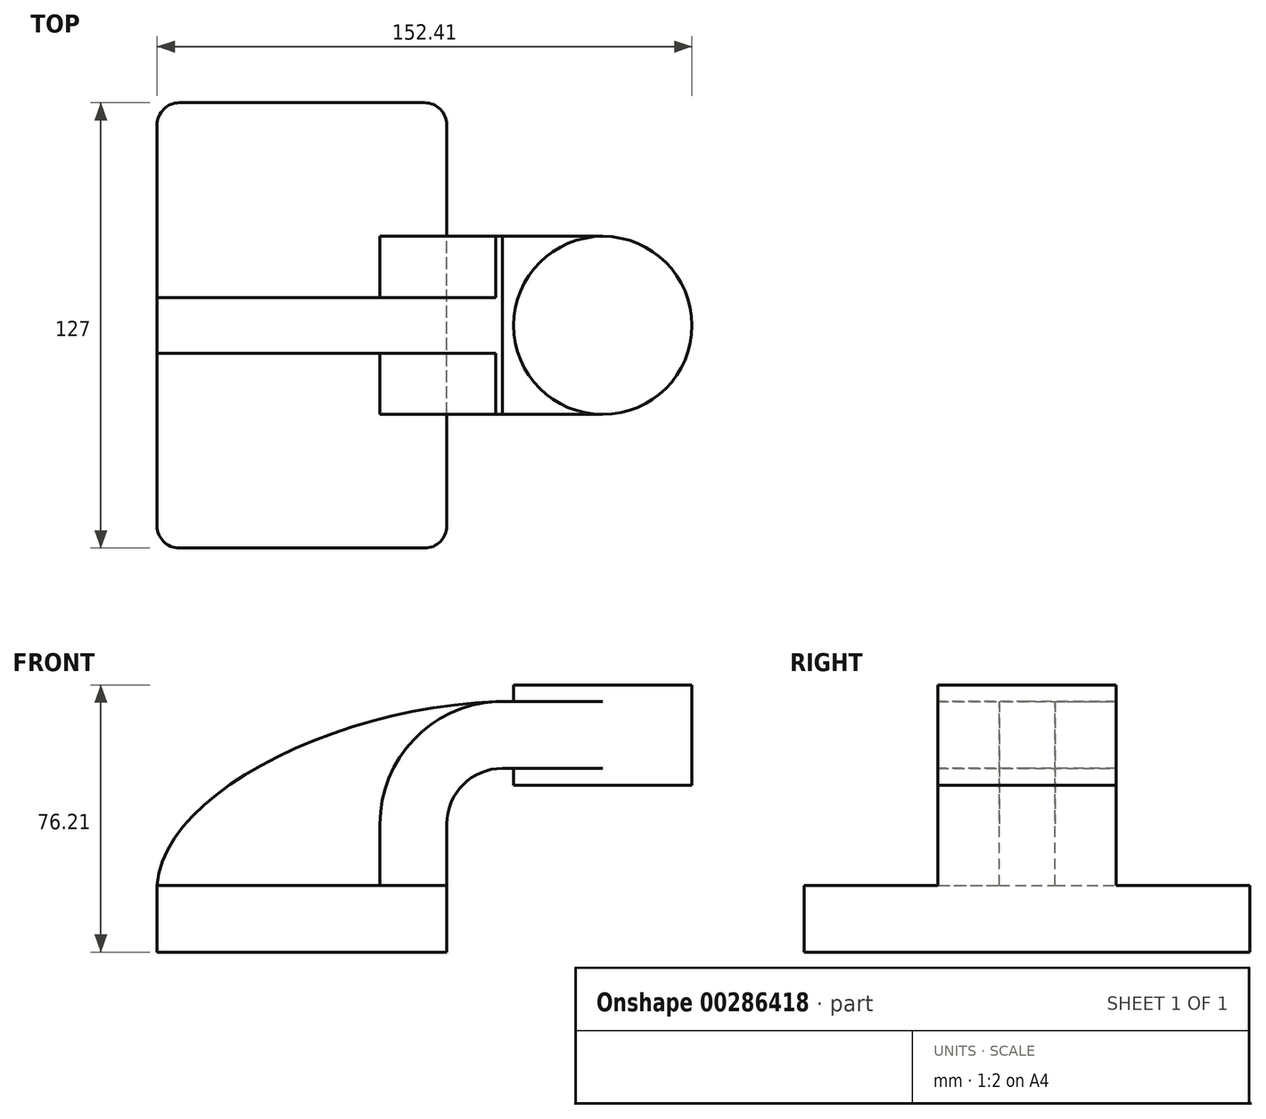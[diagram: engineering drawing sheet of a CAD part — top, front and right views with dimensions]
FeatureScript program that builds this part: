
annotation { "Feature Type Name" : "Feature", "Feature Type Description" : "" }
export const myFeature = defineFeature(function(context is Context, id is Id, definition is map)
    precondition{}
    {
        {
            var Q0;
            Q0=qCreatedBy(makeId("Front.planeOp"),FACE);
            var sketch = newSketch(context, id + "F0", { "sketchPlane" : qUnion([Q0])});
            skLineSegment(sketch, "E0.bottom", {"start": v(-41.27, -9.53) * mm, "end": v(41.28, -9.53) * mm});
            skLineSegment(sketch, "E0.top", {"start": v(-41.28, 9.52) * mm, "end": v(41.28, 9.52) * mm});
            skLineSegment(sketch, "E0.left", {"start": v(-41.28, -9.53) * mm, "end": v(-41.28, 9.52) * mm});
            skLineSegment(sketch, "E0.right", {"start": v(41.28, -9.53) * mm, "end": v(41.28, 9.52) * mm});
            skPoint(sketch, "E0.middle", {"position": v(0, 0) * mm});
            skLineSegment(sketch, "E1.bottom", {"start": v(60.32, 38.1) * mm, "end": v(111.12, 38.1) * mm});
            skLineSegment(sketch, "E1.top", {"start": v(60.32, 66.67) * mm, "end": v(111.12, 66.67) * mm});
            skLineSegment(sketch, "E1.left", {"start": v(60.32, 38.1) * mm, "end": v(60.32, 66.67) * mm});
            skLineSegment(sketch, "E1.right", {"start": v(111.12, 38.1) * mm, "end": v(111.12, 66.67) * mm});
            skPoint(sketch, "E1.middle", {"position": v(85.72, 52.39) * mm});
            skLineSegment(sketch, "E2", {"start": v(41.27, 9.52) * mm, "end": v(41.27, 27) * mm});
            skArc(sketch, "E3", {"start": v(41.27, 27) * mm, "mid": v(45.92, 38.23) * mm, "end": v(57.15, 42.88) * mm});
            skLineSegment(sketch, "E4", {"start": v(57.15, 42.88) * mm, "end": v(85.72, 42.88) * mm});
            skLineSegment(sketch, "E5.0", {"start": v(57.15, 61.93) * mm, "end": v(85.72, 61.93) * mm});
            skArc(sketch, "E5.1", {"start": v(22.22, 27) * mm, "mid": v(32.45, 51.7) * mm, "end": v(57.15, 61.93) * mm});
            skLineSegment(sketch, "E5.2", {"start": v(22.22, 9.52) * mm, "end": v(22.22, 27) * mm});
            skLineSegment(sketch, "E6", {"start": v(85.72, 38.1) * mm, "end": v(85.72, 66.67) * mm});
            skFitSpline(sketch, "E7", {"points": [v(-41.28, 9.53) * mm, v(57.15, 61.93) * mm], "startDerivative": vector(4.86, 79.85) * mm, "endDerivative": vector(136.77, 2.72) * mm});
            skSolve(sketch);
        }
        {
            var Q0;
            Q0=makeQuery(id+"F0.imprint","IMPRINT",FACE,{"disambiguationData":[TD([[makeQuery(id+"F0.imprint","IMPRINT",EDGE,{"derivedFrom":sQuery(id+"F0.wireOp",EDGE,"E0.bottom")}),1.0]])]});
            extrude(context, id + "F1", {"entities" : qUnion([Q0]), "endBound" : BoundingType.SYMMETRIC, "depth" : 127 * mm});
        }
        {
            var Q0;
            {var subQ1=sQuery(id+"F0.wireOp",EDGE,"E2");Q0=makeQuery(id+"F0.imprint","IMPRINT",FACE,{"disambiguationData":[TD([[makeQuery(id+"F0.imprint","IMPRINT",EDGE,{"derivedFrom":subQ1}),1.0]])]});}
            var Q1;
            {var subQ0=sQuery(id+"F0.wireOp",EDGE,"E4");var subQ1=sQuery(id+"F0.wireOp",EDGE,"E1.left");var subQ2=makeQuery(id+"F0.imprint","INTERSECT",VERTEX,{"derivedFrom":[subQ1,subQ0]});Q1=makeQuery(id+"F0.imprint","IMPRINT",FACE,{"disambiguationData":[TD([[makeQuery(id+"F0.imprint","IMPRINT",EDGE,{"disambiguationData":[TD([[subQ2,-1.0]])],"derivedFrom":subQ1}),-1.0]])]});}
            extrude(context, id + "F2", {"entities" : qUnion([Q0, Q1]), "operationType" : NewBodyOperationType.ADD, "endBound" : BoundingType.SYMMETRIC, "depth" : 50.8 * mm});
        }
        {
            var Q0;
            {var subQ3=sQuery(id+"F0.wireOp",EDGE,"E5.2");Q0=makeQuery(id+"F0.imprint","IMPRINT",FACE,{"disambiguationData":[TD([[makeQuery(id+"F0.imprint","IMPRINT",EDGE,{"derivedFrom":subQ3}),1.0]])]});}
            extrude(context, id + "F3", {"entities" : qUnion([Q0]), "operationType" : NewBodyOperationType.ADD, "endBound" : BoundingType.SYMMETRIC, "depth" : 15.88 * mm});
        }
        {
            var Q0;
            {var subQ4=sQuery(id+"F0.wireOp",EDGE,"E1.right");Q0=makeQuery(id+"F0.imprint","IMPRINT",FACE,{"disambiguationData":[TD([[makeQuery(id+"F0.imprint","IMPRINT",EDGE,{"derivedFrom":subQ4}),1.0]])]});}
            var Q1;
            Q1=sQuery(id+"F0.wireOp",EDGE,"E6");
            revolve(context, id + "F4", {"operationType" : NewBodyOperationType.ADD, "entities" : qUnion([Q0]), "axis" : qUnion([Q1]), "revolveType" : RevolveType.FULL});
        }
        {
            var Q0;
            Q0=makeQuery(id+"F1.opExtrude","CAP_EDGE",EDGE,{"disambiguationData":[OSD([sQuery(id+"F0.wireOp",EDGE,"E0.right")])],"isStart":false});
            var Q1;
            Q1=makeQuery(id+"F1.opExtrude","CAP_EDGE",EDGE,{"disambiguationData":[OSD([sQuery(id+"F0.wireOp",EDGE,"E0.right")])],"isStart":true});
            var Q2;
            Q2=makeQuery(id+"F1.opExtrude","CAP_EDGE",EDGE,{"disambiguationData":[OSD([sQuery(id+"F0.wireOp",EDGE,"E0.left")])],"isStart":true});
            var Q3;
            Q3=makeQuery(id+"F1.opExtrude","CAP_EDGE",EDGE,{"disambiguationData":[OSD([sQuery(id+"F0.wireOp",EDGE,"E0.left")])],"isStart":false});
            fillet(context, id + "F5", {"entities" : qUnion([Q0, Q1, Q2, Q3]), "radius" : 6.35 * mm, "tangentPropagation" : true, "allowEdgeOverflow" : false});
        }
    });
